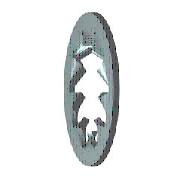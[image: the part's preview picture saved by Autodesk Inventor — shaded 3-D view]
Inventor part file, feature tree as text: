
AUTODESK INVENTOR PART (.ipt)
format: ipt  version: 2015 (Build 190159000, 159)  size: 156,672 bytes
history: native  units: mm (DEFAULTED — no unit token found)
features: sketch x2, extrude x1, pattern_circular x1, plane x1
ambient origin geometry x7: Origin, YZ Plane, XY Plane, X Axis, Y Axis, Z Axis, Center Point
bodies: Solid1 (feature_tree), Body (feature_tree)
feature tree (5):
  extrude  "Cut"  Depth=3.5814mm
  pattern_circular  "Cuts"  [2 undecoded]
  plane  "Work Plane1"
  sketch  "Sketch1"  dims[d0=7.493mm d1=3.5814mm]
  sketch  "Sketch2"  dims[d2=0.5588mm d3=0.0mm d4=5.5372mm d5=15.0deg d6=0.5588mm d7=0.0mm d8=0.107442mm d9=60.0mm d11=360.0deg d12=0.0mm d13=0.0mm d18=0.0mm d19=0.0mm]
note: 2 required parameter values undecoded (feature->parameter linkage not recoverable at this tier; creation-order binding heuristic only, values carry confidence <= 0.55)
